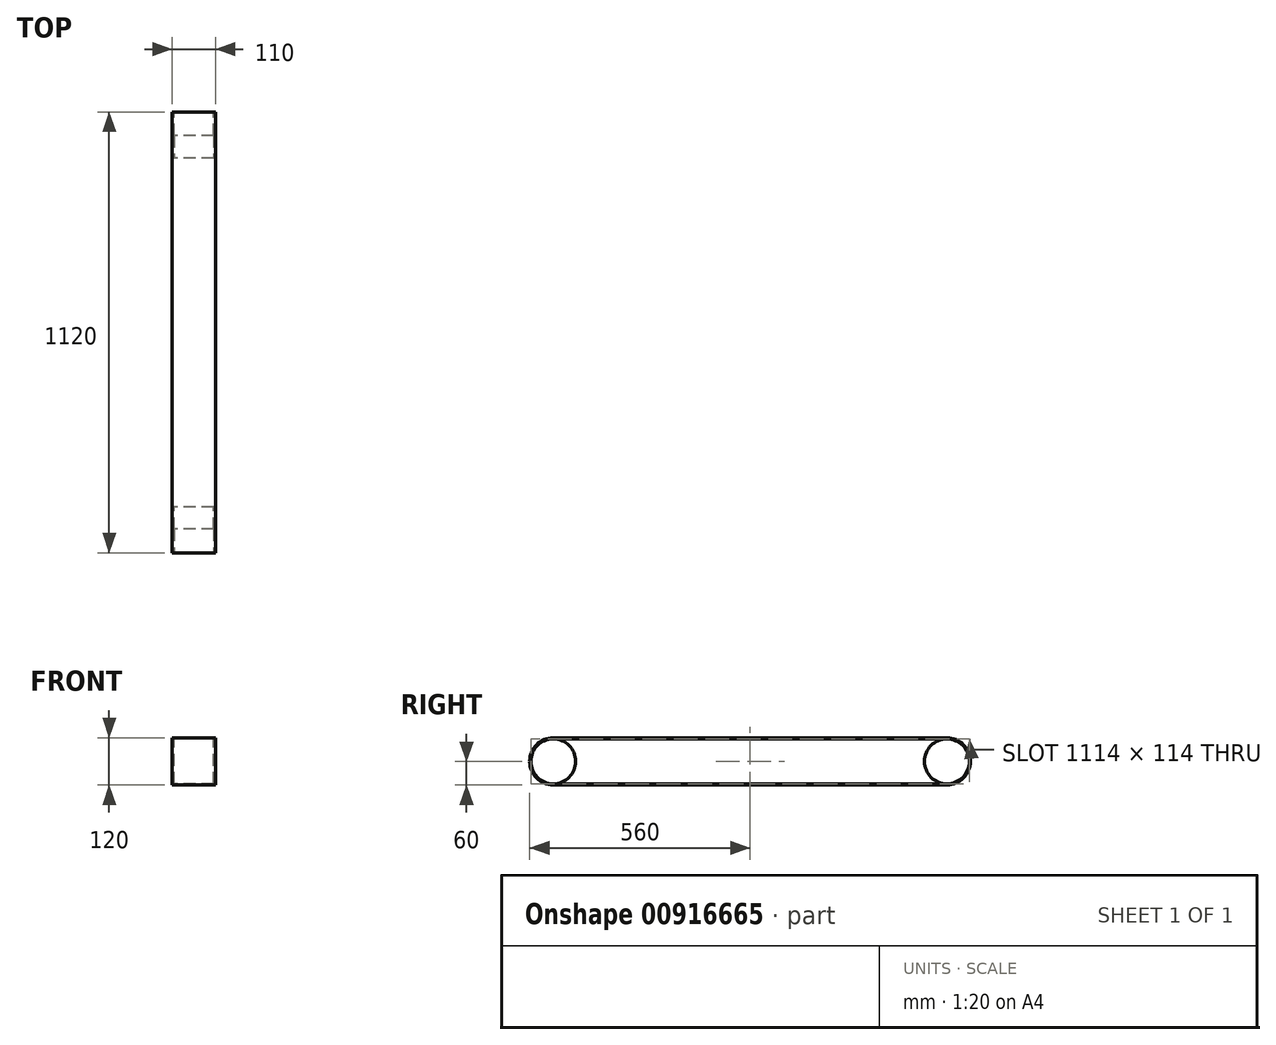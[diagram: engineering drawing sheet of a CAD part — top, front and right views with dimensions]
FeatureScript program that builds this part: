
annotation { "Feature Type Name" : "Feature", "Feature Type Description" : "" }
export const myFeature = defineFeature(function(context is Context, id is Id, definition is map)
    precondition{}
    {
        {
            var Q0;
            Q0=qCreatedBy(makeId("Right.planeOp"),FACE);
            var sketch = newSketch(context, id + "F0", { "sketchPlane" : qUnion([Q0])});
            skArc(sketch, "E0", {"start": v(0, -60) * mm, "mid": v(60, 0) * mm, "end": v(0, 60) * mm});
            skLineSegment(sketch, "E1", {"start": v(0, -60) * mm, "end": v(-1000, -60) * mm});
            skArc(sketch, "E2", {"start": v(-1000, 60) * mm, "mid": v(-1060, 0) * mm, "end": v(-1000, -60) * mm});
            skLineSegment(sketch, "E3", {"start": v(-1000, 60) * mm, "end": v(0, 60) * mm});
            skLineSegment(sketch, "E4.0", {"start": v(-1000, 57) * mm, "end": v(0, 57) * mm});
            skLineSegment(sketch, "E5.0", {"start": v(0, -57) * mm, "end": v(-1000, -57) * mm});
            skCircle(sketch, "E6.0", {"center": v(-1000, 0) * mm, "radius": 57 * mm});
            skCircle(sketch, "E7.0", {"center": v(0, 0) * mm, "radius": 57 * mm});
            skSolve(sketch);
        }
        {
            var Q0;
            {var subQ0=sQuery(id+"F0.wireOp",EDGE,"E6.0");var subQ1=makeQuery(id+"F0.imprint","INTERSECT",VERTEX,{"derivedFrom":[sQuery(id+"F0.wireOp",EDGE,"E4.0"),subQ0]});Q0=makeQuery(id+"F0.imprint","IMPRINT",FACE,{"disambiguationData":[TD([[makeQuery(id+"F0.imprint","IMPRINT",EDGE,{"disambiguationData":[TD([[subQ1,-1.0]])],"derivedFrom":subQ0}),1.0]])]});}
            var Q1;
            {var subQ0=sQuery(id+"F0.wireOp",EDGE,"E7.0");var subQ1=makeQuery(id+"F0.imprint","INTERSECT",VERTEX,{"derivedFrom":[sQuery(id+"F0.wireOp",EDGE,"E4.0"),subQ0]});Q1=makeQuery(id+"F0.imprint","IMPRINT",FACE,{"disambiguationData":[TD([[makeQuery(id+"F0.imprint","IMPRINT",EDGE,{"disambiguationData":[TD([[subQ1,-1.0]])],"derivedFrom":subQ0}),1.0]])]});}
            extrude(context, id + "F1", {"entities" : qUnion([Q0, Q1]), "depth" : 100 * mm, "offsetDistance" : 25 * mm});
        }
        {
            var Q0;
            Q0=makeQuery(id+"F0.imprint","IMPRINT",FACE,{"disambiguationData":[TD([[makeQuery(id+"F0.imprint","IMPRINT",EDGE,{"derivedFrom":sQuery(id+"F0.wireOp",EDGE,"E0")}),1.0]])]});
            extrude(context, id + "F2", {"entities" : qUnion([Q0]), "depth" : 105 * mm, "offsetDistance" : 25 * mm});
        }
        {
            var Q0;
            Q0=makeQuery(id+"F0.imprint","IMPRINT",FACE,{"disambiguationData":[TD([[makeQuery(id+"F0.imprint","IMPRINT",EDGE,{"derivedFrom":sQuery(id+"F0.wireOp",EDGE,"E0")}),1.0]])]});
            extrude(context, id + "F3", {"entities" : qUnion([Q0]), "operationType" : NewBodyOperationType.ADD, "oppositeDirection" : true, "depth" : 5 * mm, "offsetDistance" : 25 * mm});
        }
    });
